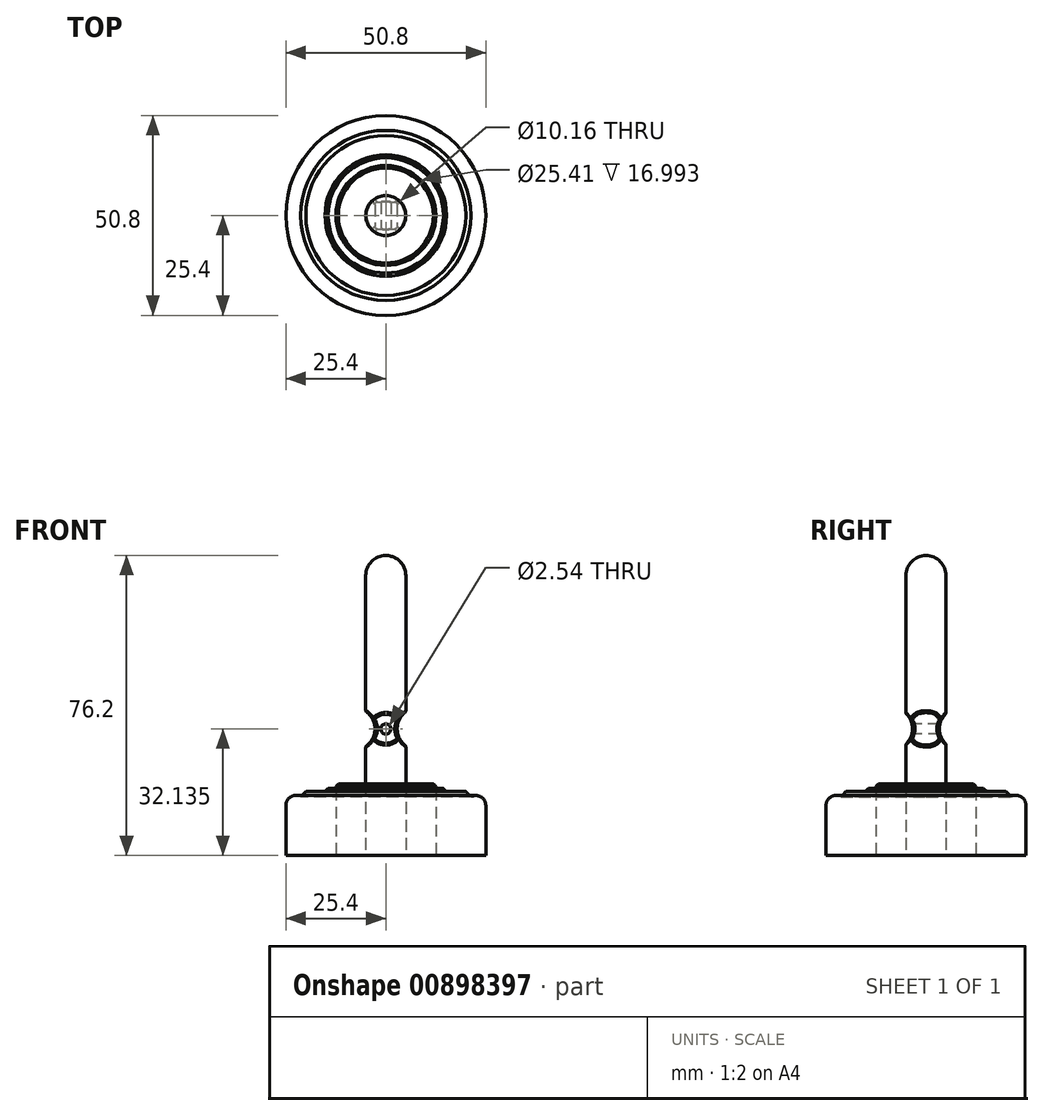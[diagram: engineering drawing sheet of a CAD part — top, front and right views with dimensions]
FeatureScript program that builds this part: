
annotation { "Feature Type Name" : "Feature", "Feature Type Description" : "" }
export const myFeature = defineFeature(function(context is Context, id is Id, definition is map)
    precondition{}
    {
        {
            var Q0;
            Q0=qCreatedBy(makeId("Top.planeOp"),FACE);
            var sketch = newSketch(context, id + "F0", { "sketchPlane" : qUnion([Q0])});
            skCircle(sketch, "E0", {"center": v(0, 0) * mm, "radius": 25.4 * mm});
            skCircle(sketch, "E1", {"center": v(0, 0) * mm, "radius": 5.08 * mm});
            skCircle(sketch, "E2", {"center": v(0, 0) * mm, "radius": 12.7 * mm});
            skCircle(sketch, "E3", {"center": v(0, 0) * mm, "radius": 19.72 * mm});
            skSolve(sketch);
        }
        {
            var Q0;
            Q0=makeQuery(id+"F0.imprint","IMPRINT",FACE,{"disambiguationData":[TD([[makeQuery(id+"F0.imprint","IMPRINT",EDGE,{"derivedFrom":sQuery(id+"F0.wireOp",EDGE,"E0")}),1.0]])]});
            extrude(context, id + "F1", {"entities" : qUnion([Q0]), "depth" : 15.24 * mm, "offsetDistance" : 25.4 * mm});
        }
        {
            var Q0;
            Q0=makeQuery(id+"F0.imprint","IMPRINT",FACE,{"disambiguationData":[TD([[makeQuery(id+"F0.imprint","IMPRINT",EDGE,{"derivedFrom":sQuery(id+"F0.wireOp",EDGE,"E1")}),1.0]])]});
            extrude(context, id + "F2", {"entities" : qUnion([Q0]), "operationType" : NewBodyOperationType.ADD, "depth" : 76.2 * mm, "offsetDistance" : 25.4 * mm});
        }
        {
            var Q0;
            Q0=makeQuery(id+"F2.opExtrude","CAP_EDGE",EDGE,{"disambiguationData":[OSD([sQuery(id+"F0.wireOp",EDGE,"E1")])],"isStart":false});
            fillet(context, id + "F3", {"entities" : qUnion([Q0]), "radius" : 5.08 * mm, "tangentPropagation" : true, "allowEdgeOverflow" : false});
        }
        {
            var Q0;
            Q0=makeQuery(id+"F1.opExtrude","CAP_EDGE",EDGE,{"disambiguationData":[OSD([sQuery(id+"F0.wireOp",EDGE,"E0")])],"isStart":false});
            fillet(context, id + "F4", {"entities" : qUnion([Q0]), "radius" : 2.54 * mm, "tangentPropagation" : true, "allowEdgeOverflow" : false});
        }
        {
            var Q0;
            Q0=makeQuery(id+"F1.opExtrude","CAP_FACE",FACE,{"disambiguationData":[OSD([sQuery(id+"F0.wireOp",EDGE,"E0"),sQuery(id+"F0.wireOp",EDGE,"E3")])],"isStart":false});
            extrude(context, id + "F5", {"entities" : qUnion([Q0]), "operationType" : NewBodyOperationType.ADD, "depth" : 0.97 * mm, "offsetDistance" : 25.4 * mm});
        }
        {
            var Q0;
            Q0=makeQuery(id+"F0.imprint","IMPRINT",FACE,{"disambiguationData":[TD([[makeQuery(id+"F0.imprint","IMPRINT",EDGE,{"derivedFrom":sQuery(id+"F0.wireOp",EDGE,"E2")}),-1.0]])]});
            extrude(context, id + "F6", {"entities" : qUnion([Q0]), "operationType" : NewBodyOperationType.ADD, "depth" : 17 * mm, "offsetDistance" : 25.4 * mm});
        }
        {
            var Q0;
            Q0=makeQuery(id+"F0.imprint","IMPRINT",FACE,{"disambiguationData":[TD([[makeQuery(id+"F0.imprint","IMPRINT",EDGE,{"derivedFrom":sQuery(id+"F0.wireOp",EDGE,"E1")}),-1.0]])]});
            extrude(context, id + "F7", {"entities" : qUnion([Q0]), "depth" : 18.21 * mm, "offsetDistance" : 25.4 * mm});
        }
        {
            var Q0;
            Q0=makeQuery(id+"F6.opExtrude","CAP_EDGE",EDGE,{"disambiguationData":[OSD([sQuery(id+"F0.wireOp",EDGE,"E3")])],"isStart":false});
            chamfer(context, id + "F8", {"entities" : qUnion([Q0]), "width" : 5.08 * mm, "tangentPropagation" : true});
        }
        {
            var Q0;
            Q0=makeQuery(id+"F5.opExtrude","CAP_EDGE",EDGE,{"disambiguationData":[OSD([sQuery(id+"F0.wireOp",EDGE,"E0"),sQuery(id+"F0.wireOp",EDGE,"E3")])],"isStart":false});
            chamfer(context, id + "F9", {"entities" : qUnion([Q0]), "width" : 2.54 * mm, "tangentPropagation" : true});
        }
        {
            var Q0;
            Q0=makeQuery(id+"F7.opExtrude","CAP_EDGE",EDGE,{"disambiguationData":[OSD([sQuery(id+"F0.wireOp",EDGE,"E2")])],"isStart":false});
            chamfer(context, id + "F10", {"entities" : qUnion([Q0]), "width" : 0.64 * mm, "tangentPropagation" : true});
        }
        {
            var Q0;
            Q0=qCreatedBy(makeId("Front.planeOp"),FACE);
            cPlane(context, id + "F11", {"entities" : qUnion([Q0]), "cplaneType" : CPlaneType.OFFSET, "offset" : 25.4 * mm, "width" : 152.4 * mm, "height" : 152.4 * mm});
        }
        {
            var Q0;
            Q0=qCreatedBy(id+"F11.planeOp",FACE);
            var sketch = newSketch(context, id + "F12", { "sketchPlane" : qUnion([Q0])});
            skCircle(sketch, "E4", {"center": v(0, 32.14) * mm, "radius": 1.27 * mm});
            skSolve(sketch);
        }
        {
            var Q0;
            Q0=makeQuery(id+"F12.imprint","IMPRINT",FACE,{"disambiguationData":[TD([[makeQuery(id+"F12.imprint","IMPRINT",EDGE,{"derivedFrom":sQuery(id+"F12.wireOp",EDGE,"E4")}),1.0]])]});
            var Q1;
            Q1=sQuery(id+"F12.wireOp",EDGE,"E4");
            extrude(context, id + "F13", {"entities" : qUnion([Q0]), "operationType" : NewBodyOperationType.REMOVE, "surfaceEntities" : qUnion([Q1]), "oppositeDirection" : true, "depth" : 37.34 * mm, "offsetDistance" : 25.4 * mm});
        }
        {
            var Q0;
            Q0=qCreatedBy(id+"F11.planeOp",FACE);
            var sketch = newSketch(context, id + "F14", { "sketchPlane" : qUnion([Q0])});
            skCircle(sketch, "E5", {"center": v(8.23, 32.16) * mm, "radius": 5.33 * mm});
            skCircle(sketch, "E6", {"center": v(-8.1, 32.16) * mm, "radius": 5.33 * mm});
            skSolve(sketch);
        }
        {
            var Q0;
            Q0=makeQuery(id+"F14.imprint","IMPRINT",FACE,{"disambiguationData":[TD([[makeQuery(id+"F14.imprint","IMPRINT",EDGE,{"derivedFrom":sQuery(id+"F14.wireOp",EDGE,"E5")}),1.0]])]});
            var Q1;
            Q1=makeQuery(id+"F14.imprint","IMPRINT",FACE,{"disambiguationData":[TD([[makeQuery(id+"F14.imprint","IMPRINT",EDGE,{"derivedFrom":sQuery(id+"F14.wireOp",EDGE,"E6")}),1.0]])]});
            var Q2;
            Q2=sQuery(id+"F14.wireOp",EDGE,"E5");
            var Q3;
            Q3=sQuery(id+"F14.wireOp",EDGE,"E6");
            extrude(context, id + "F15", {"entities" : qUnion([Q0, Q1]), "operationType" : NewBodyOperationType.REMOVE, "surfaceEntities" : qUnion([Q2, Q3]), "oppositeDirection" : true, "depth" : 39.88 * mm, "offsetDistance" : 25.4 * mm});
        }
        {
            var Q0;
            Q0=qCreatedBy(makeId("Right.planeOp"),FACE);
            cPlane(context, id + "F16", {"entities" : qUnion([Q0]), "cplaneType" : CPlaneType.OFFSET, "offset" : 25.4 * mm, "width" : 152.4 * mm, "height" : 152.4 * mm});
        }
        {
            var Q0;
            Q0=qCreatedBy(id+"F16.planeOp",FACE);
            var sketch = newSketch(context, id + "F17", { "sketchPlane" : qUnion([Q0])});
            skCircle(sketch, "E7", {"center": v(-8.76, 32.18) * mm, "radius": 5.33 * mm});
            skCircle(sketch, "E8", {"center": v(8.74, 32.18) * mm, "radius": 5.33 * mm});
            skSolve(sketch);
        }
        {
            var Q0;
            Q0=makeQuery(id+"F17.imprint","IMPRINT",FACE,{"disambiguationData":[TD([[makeQuery(id+"F17.imprint","IMPRINT",EDGE,{"derivedFrom":sQuery(id+"F17.wireOp",EDGE,"E7")}),1.0]])]});
            var Q1;
            Q1=makeQuery(id+"F17.imprint","IMPRINT",FACE,{"disambiguationData":[TD([[makeQuery(id+"F17.imprint","IMPRINT",EDGE,{"derivedFrom":sQuery(id+"F17.wireOp",EDGE,"E8")}),1.0]])]});
            extrude(context, id + "F18", {"entities" : qUnion([Q0, Q1]), "operationType" : NewBodyOperationType.REMOVE, "oppositeDirection" : true, "depth" : 42.57 * mm, "offsetDistance" : 25.4 * mm});
        }
        {
            var Q0;
            Q0=makeQuery(id+"F18.boolean.opBoolean","INTERSECT",EDGE,{"derivedFrom":[makeQuery(id+"F15.boolean.opBoolean","COPY",FACE,{"derivedFrom":makeQuery(id+"F15.opExtrude","SWEPT_FACE",FACE,{"disambiguationData":[OSD([sQuery(id+"F14.wireOp",EDGE,"E5")])]})}),makeQuery(id+"F18.opExtrude","SWEPT_FACE",FACE,{"disambiguationData":[OSD([sQuery(id+"F17.wireOp",EDGE,"E8")])]})]});
            fillet(context, id + "F19", {"entities" : qUnion([Q0]), "radius" : 0.64 * mm, "tangentPropagation" : true, "allowEdgeOverflow" : false});
        }
        {
            var Q0;
            Q0=makeQuery(id+"F18.boolean.opBoolean","INTERSECT",EDGE,{"derivedFrom":[makeQuery(id+"F15.boolean.opBoolean","COPY",FACE,{"derivedFrom":makeQuery(id+"F15.opExtrude","SWEPT_FACE",FACE,{"disambiguationData":[OSD([sQuery(id+"F14.wireOp",EDGE,"E5")])]})}),makeQuery(id+"F18.opExtrude","SWEPT_FACE",FACE,{"disambiguationData":[OSD([sQuery(id+"F17.wireOp",EDGE,"E7")])]})]});
            fillet(context, id + "F20", {"entities" : qUnion([Q0]), "radius" : 0.64 * mm, "tangentPropagation" : true, "allowEdgeOverflow" : false});
        }
        {
            var Q0;
            Q0=makeQuery(id+"F18.boolean.opBoolean","INTERSECT",EDGE,{"derivedFrom":[makeQuery(id+"F15.boolean.opBoolean","COPY",FACE,{"derivedFrom":makeQuery(id+"F15.opExtrude","SWEPT_FACE",FACE,{"disambiguationData":[OSD([sQuery(id+"F14.wireOp",EDGE,"E6")])]})}),makeQuery(id+"F18.opExtrude","SWEPT_FACE",FACE,{"disambiguationData":[OSD([sQuery(id+"F17.wireOp",EDGE,"E7")])]})]});
            fillet(context, id + "F21", {"entities" : qUnion([Q0]), "radius" : 0.64 * mm, "tangentPropagation" : true, "allowEdgeOverflow" : false});
        }
        {
            var Q0;
            Q0=makeQuery(id+"F18.boolean.opBoolean","INTERSECT",EDGE,{"derivedFrom":[makeQuery(id+"F15.boolean.opBoolean","COPY",FACE,{"derivedFrom":makeQuery(id+"F15.opExtrude","SWEPT_FACE",FACE,{"disambiguationData":[OSD([sQuery(id+"F14.wireOp",EDGE,"E6")])]})}),makeQuery(id+"F18.opExtrude","SWEPT_FACE",FACE,{"disambiguationData":[OSD([sQuery(id+"F17.wireOp",EDGE,"E8")])]})]});
            fillet(context, id + "F22", {"entities" : qUnion([Q0]), "radius" : 0.64 * mm, "tangentPropagation" : true, "allowEdgeOverflow" : false});
        }
        {
            var Q0;
            Q0=makeQuery(id+"F18.boolean.opBoolean","INTERSECT",EDGE,{"disambiguationData":[OD(0.0)],"derivedFrom":[makeQuery(id+"F2.opExtrude","SWEPT_FACE",FACE,{"disambiguationData":[OSD([sQuery(id+"F0.wireOp",EDGE,"E1")])]}),makeQuery(id+"F18.opExtrude","SWEPT_FACE",FACE,{"disambiguationData":[OSD([sQuery(id+"F17.wireOp",EDGE,"E8")])]})]});
            var Q1;
            Q1=makeQuery(id+"F18.boolean.opBoolean","SPLIT",EDGE,{"disambiguationData":[OD(0.0)],"derivedFrom":makeQuery(id+"F15.boolean.opBoolean","INTERSECT",EDGE,{"derivedFrom":[makeQuery(id+"F2.opExtrude","SWEPT_FACE",FACE,{"disambiguationData":[OSD([sQuery(id+"F0.wireOp",EDGE,"E1")])]}),makeQuery(id+"F15.opExtrude","SWEPT_FACE",FACE,{"disambiguationData":[OSD([sQuery(id+"F14.wireOp",EDGE,"E6")])]})]})});
            var Q2;
            Q2=makeQuery(id+"F18.boolean.opBoolean","SPLIT",EDGE,{"disambiguationData":[OD(1.0)],"derivedFrom":makeQuery(id+"F15.boolean.opBoolean","INTERSECT",EDGE,{"derivedFrom":[makeQuery(id+"F2.opExtrude","SWEPT_FACE",FACE,{"disambiguationData":[OSD([sQuery(id+"F0.wireOp",EDGE,"E1")])]}),makeQuery(id+"F15.opExtrude","SWEPT_FACE",FACE,{"disambiguationData":[OSD([sQuery(id+"F14.wireOp",EDGE,"E6")])]})]})});
            var Q3;
            Q3=makeQuery(id+"F18.boolean.opBoolean","INTERSECT",EDGE,{"disambiguationData":[OD(1.0)],"derivedFrom":[makeQuery(id+"F2.opExtrude","SWEPT_FACE",FACE,{"disambiguationData":[OSD([sQuery(id+"F0.wireOp",EDGE,"E1")])]}),makeQuery(id+"F18.opExtrude","SWEPT_FACE",FACE,{"disambiguationData":[OSD([sQuery(id+"F17.wireOp",EDGE,"E8")])]})]});
            var Q4;
            Q4=makeQuery(id+"F18.boolean.opBoolean","SPLIT",EDGE,{"disambiguationData":[OD(0.0)],"derivedFrom":makeQuery(id+"F15.boolean.opBoolean","INTERSECT",EDGE,{"derivedFrom":[makeQuery(id+"F2.opExtrude","SWEPT_FACE",FACE,{"disambiguationData":[OSD([sQuery(id+"F0.wireOp",EDGE,"E1")])]}),makeQuery(id+"F15.opExtrude","SWEPT_FACE",FACE,{"disambiguationData":[OSD([sQuery(id+"F14.wireOp",EDGE,"E5")])]})]})});
            var Q5;
            Q5=makeQuery(id+"F18.boolean.opBoolean","SPLIT",EDGE,{"disambiguationData":[OD(1.0)],"derivedFrom":makeQuery(id+"F15.boolean.opBoolean","INTERSECT",EDGE,{"derivedFrom":[makeQuery(id+"F2.opExtrude","SWEPT_FACE",FACE,{"disambiguationData":[OSD([sQuery(id+"F0.wireOp",EDGE,"E1")])]}),makeQuery(id+"F15.opExtrude","SWEPT_FACE",FACE,{"disambiguationData":[OSD([sQuery(id+"F14.wireOp",EDGE,"E5")])]})]})});
            fillet(context, id + "F23", {"entities" : qUnion([Q0, Q1, Q2, Q3, Q4, Q5]), "radius" : 0.64 * mm, "tangentPropagation" : true, "allowEdgeOverflow" : false});
        }
    });
